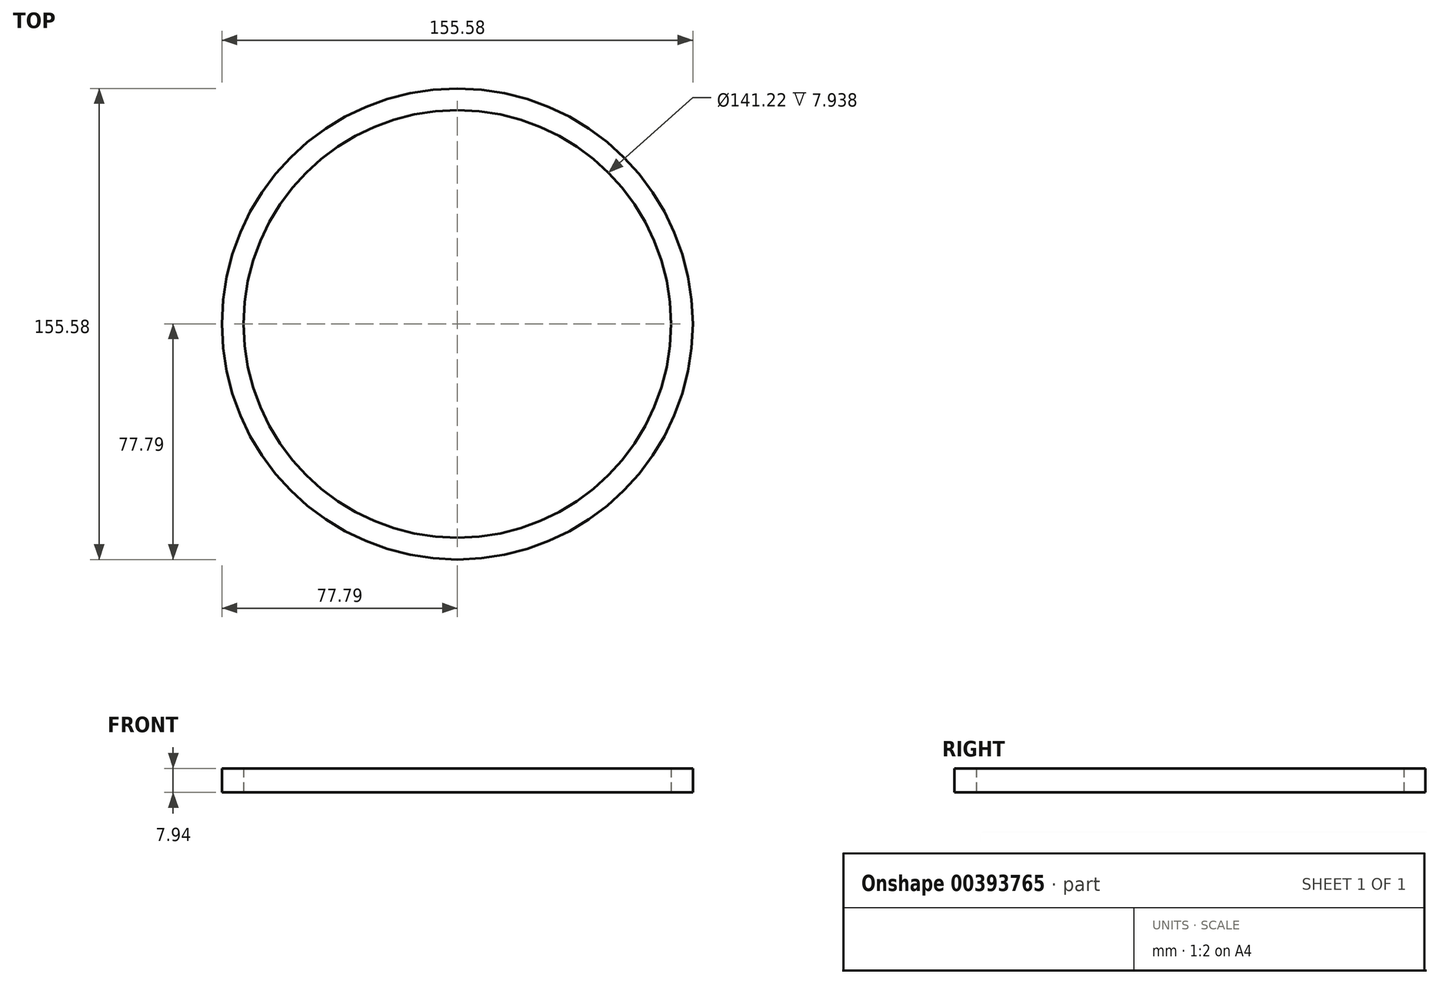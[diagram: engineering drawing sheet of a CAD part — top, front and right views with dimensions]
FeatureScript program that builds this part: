
annotation { "Feature Type Name" : "Feature", "Feature Type Description" : "" }
export const myFeature = defineFeature(function(context is Context, id is Id, definition is map)
    precondition{}
    {
        {
            var Q0;
            Q0=qCreatedBy(makeId("Top.planeOp"),FACE);
            var sketch = newSketch(context, id + "F0", { "sketchPlane" : qUnion([Q0])});
            skCircle(sketch, "E0", {"center": v(0, 0) * mm, "radius": 77.79 * mm});
            skSolve(sketch);
        }
        {
            var Q0;
            Q0=makeQuery(id+"F0.imprint","IMPRINT",FACE,{"disambiguationData":[TD([[makeQuery(id+"F0.imprint","IMPRINT",EDGE,{"derivedFrom":sQuery(id+"F0.wireOp",EDGE,"E0")}),1.0]])]});
            var sketch = newSketch(context, id + "F1", { "sketchPlane" : qUnion([Q0])});
            skCircle(sketch, "E1", {"center": v(0, 0) * mm, "radius": 70.61 * mm});
            skSolve(sketch);
        }
        {
            var Q0;
            Q0=makeQuery(id+"F1.imprint","IMPRINT",FACE,{"disambiguationData":[TD([[makeQuery(id+"F1.imprint","IMPRINT",EDGE,{"derivedFrom":sQuery(id+"F1.wireOp",EDGE,"E1")}),-1.0]])]});
            extrude(context, id + "F2", {"entities" : qUnion([Q0]), "depth" : 7.94 * mm});
        }
    });
